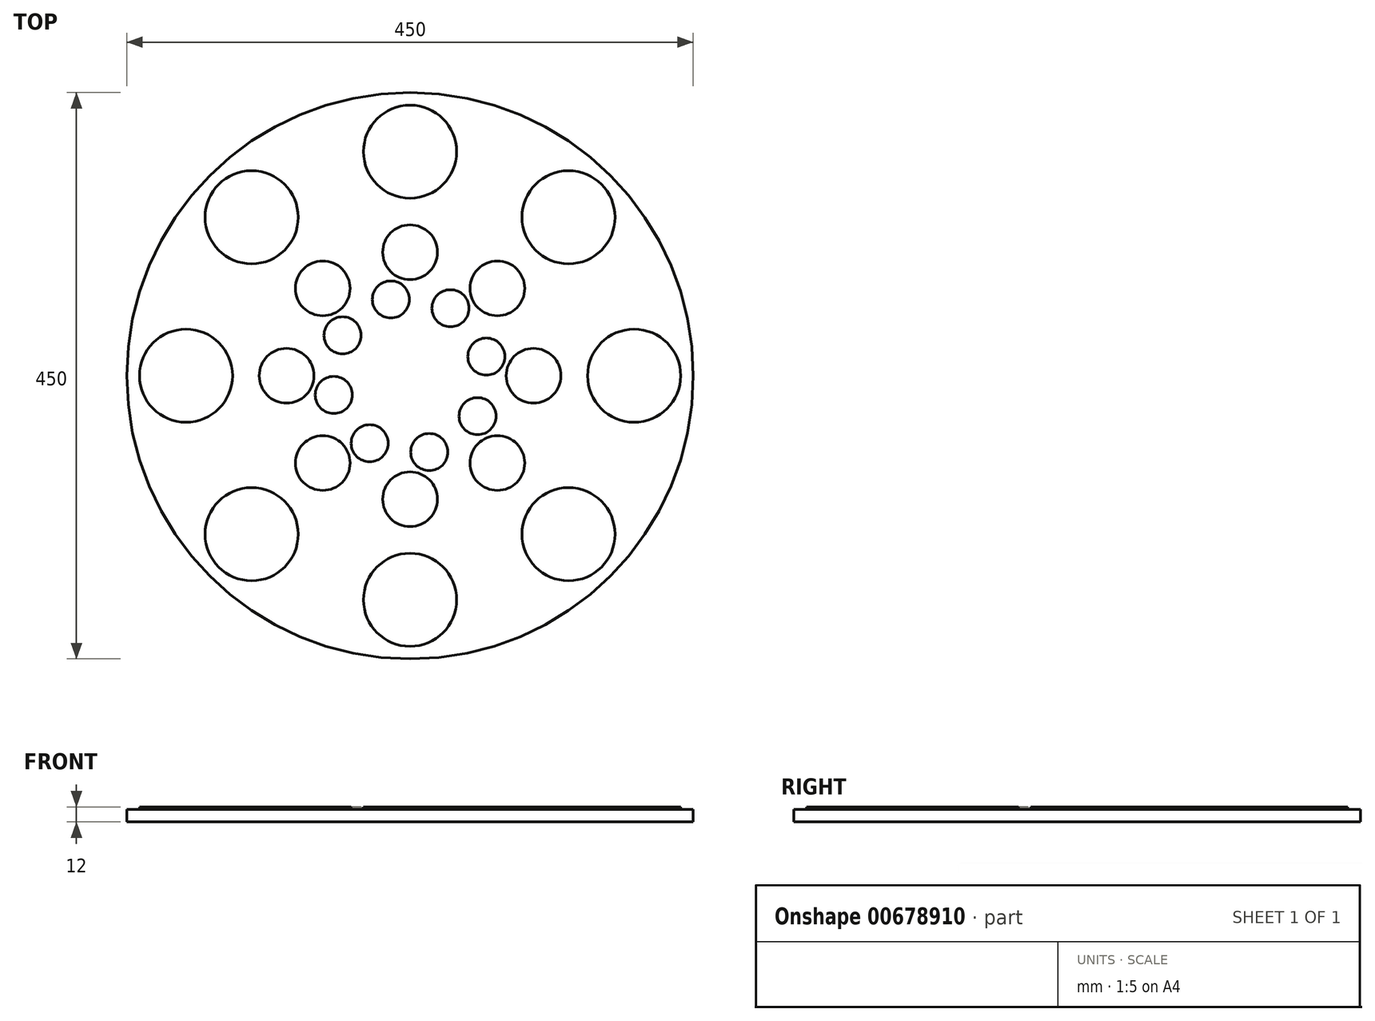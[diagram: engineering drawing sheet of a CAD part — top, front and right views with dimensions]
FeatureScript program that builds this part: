
annotation { "Feature Type Name" : "Feature", "Feature Type Description" : "" }
export const myFeature = defineFeature(function(context is Context, id is Id, definition is map)
    precondition{}
    {
        {
            var Q0;
            Q0=qCreatedBy(makeId("Top.planeOp"),FACE);
            var sketch = newSketch(context, id + "F0", { "sketchPlane" : qUnion([Q0])});
            skCircle(sketch, "E0", {"center": v(0, 0) * mm, "radius": 225 * mm});
            skSolve(sketch);
        }
        {
            var Q0;
            Q0 = qSketchRegion(id + "F0", true);
            extrude(context, id + "F1", {"entities" : qUnion([Q0]), "depth" : 10 * mm, "offsetDistance" : 25 * mm});
        }
        {
            var Q0;
            Q0=makeQuery(id+"F1.opExtrude","CAP_FACE",FACE,{"disambiguationData":[OSD([sQuery(id+"F0.wireOp",EDGE,"E0")])],"isStart":false});
            var sketch = newSketch(context, id + "F2", { "sketchPlane" : qUnion([Q0])});
            skCircle(sketch, "E1", {"center": v(0, 178.01) * mm, "radius": 36.99 * mm});
            skCircle(sketch, "E2", {"center": v(0, 98.12) * mm, "radius": 21.75 * mm});
            skCircle(sketch, "E3", {"center": v(-15.24, 60.62) * mm, "radius": 14.72 * mm});
            skSolve(sketch);
        }
        {
            var Q0;
            Q0 = qSketchRegion(id + "F2", true);
            extrude(context, id + "F3", {"entities" : qUnion([Q0]), "depth" : 2 * mm, "offsetDistance" : 25 * mm});
        }
        {
            var Q0;
            Q0=qCreatedBy(makeId("Right.planeOp"),FACE);
            var sketch = newSketch(context, id + "F4", { "sketchPlane" : qUnion([Q0])});
            skLineSegment(sketch, "E4", {"start": v(0, 0) * mm, "end": v(0, 83.77) * mm, "construction": true});
            skSolve(sketch);
        }
        {
            var Q0;
            Q0=makeQuery(id+"F3.opExtrude","SWEPT_BODY",BODY,{"disambiguationData":[OSD([sQuery(id+"F2.wireOp",EDGE,"E1")])]});
            var Q1;
            Q1=makeQuery(id+"F3.opExtrude","SWEPT_BODY",BODY,{"disambiguationData":[OSD([sQuery(id+"F2.wireOp",EDGE,"E3")])]});
            var Q2;
            Q2=makeQuery(id+"F3.opExtrude","SWEPT_BODY",BODY,{"disambiguationData":[OSD([sQuery(id+"F2.wireOp",EDGE,"E2")])]});
            var Q3;
            Q3=sQuery(id+"F4.wireOp",EDGE,"E4");
            circularPattern(context, id + "F5", {"entities" : qUnion([Q0, Q1, Q2]), "axis" : qUnion([Q3]), "angle" : 360 * degree, "instanceCount" : 8, "equalSpace" : true});
        }
    });
